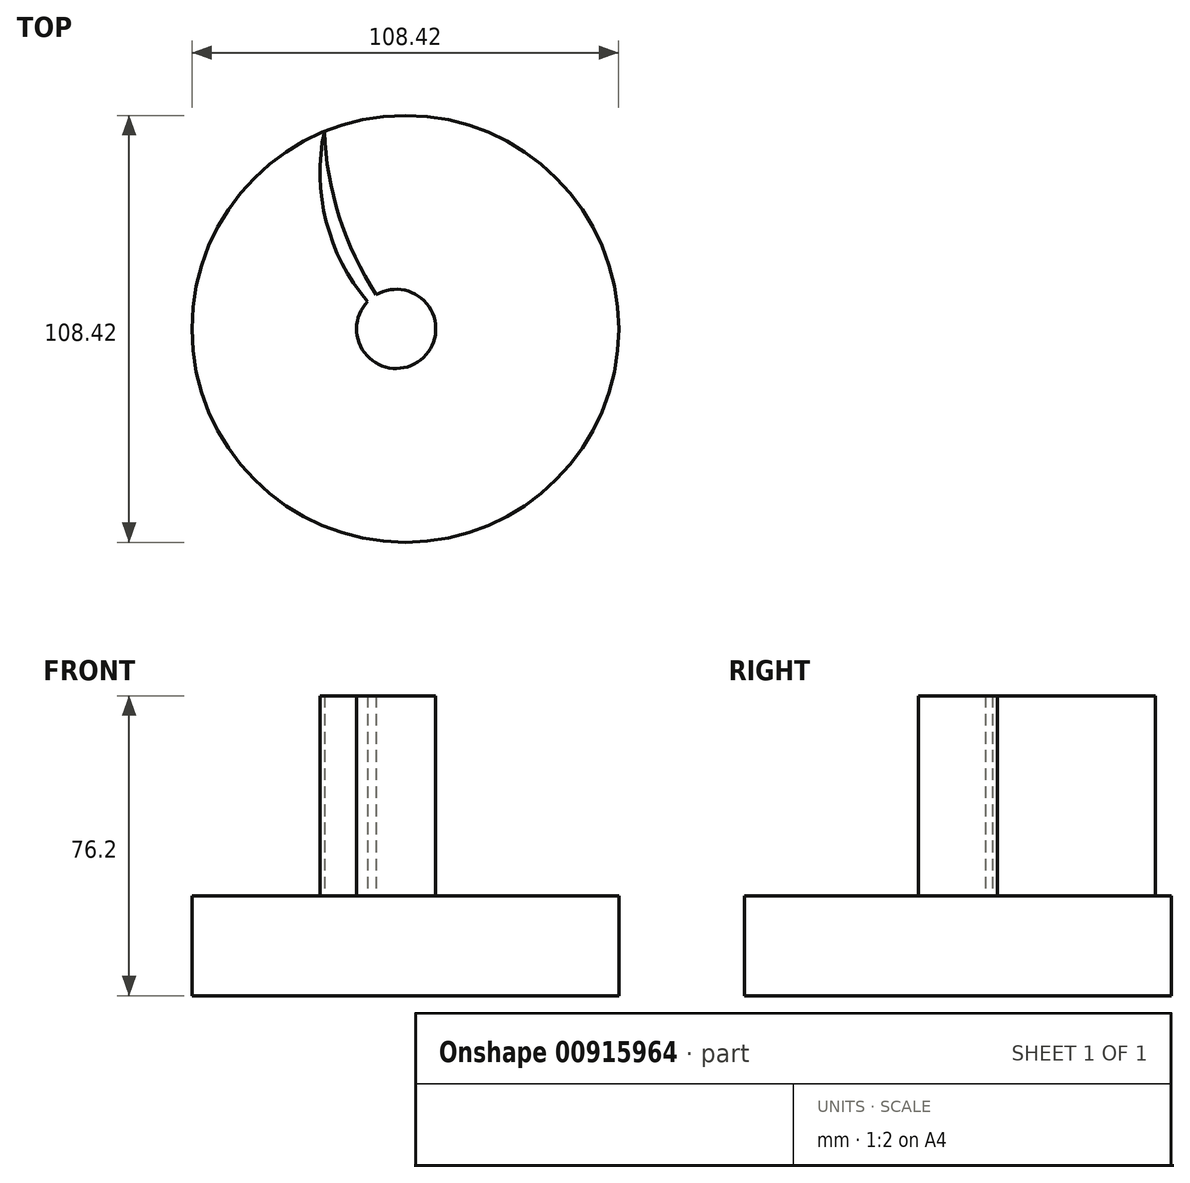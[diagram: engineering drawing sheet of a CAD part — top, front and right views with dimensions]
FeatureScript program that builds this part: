
annotation { "Feature Type Name" : "Feature", "Feature Type Description" : "" }
export const myFeature = defineFeature(function(context is Context, id is Id, definition is map)
    precondition{}
    {
        {
            var Q0;
            Q0=qCreatedBy(makeId("Top.planeOp"),FACE);
            var sketch = newSketch(context, id + "F0", { "sketchPlane" : qUnion([Q0])});
            skCircle(sketch, "E0", {"center": v(0, 0) * mm, "radius": 54.21 * mm});
            skSolve(sketch);
        }
        {
            var Q0;
            Q0=makeQuery(id+"F0.imprint","IMPRINT",FACE,{"disambiguationData":[TD([[makeQuery(id+"F0.imprint","IMPRINT",EDGE,{"derivedFrom":sQuery(id+"F0.wireOp",EDGE,"E0")}),1.0]])]});
            extrude(context, id + "F1", {"entities" : qUnion([Q0]), "depth" : 25.4 * mm, "offsetDistance" : 25.4 * mm});
        }
        {
            var Q0;
            Q0=makeQuery(id+"F1.opExtrude","CAP_FACE",FACE,{"disambiguationData":[OSD([sQuery(id+"F0.wireOp",EDGE,"E0")])],"isStart":false});
            var sketch = newSketch(context, id + "F2", { "sketchPlane" : qUnion([Q0])});
            skArc(sketch, "E1", {"start": v(-20.6, 50.15) * mm, "mid": v(-20.1, 27.28) * mm, "end": v(-9.6, 6.97) * mm});
            skArc(sketch, "E2", {"start": v(-20.6, 50.15) * mm, "mid": v(-16.79, 28.53) * mm, "end": v(-7.42, 8.68) * mm});
            skArc(sketch, "E3", {"start": v(-9.6, 6.97) * mm, "mid": v(3.9, -7.9) * mm, "end": v(-7.42, 8.68) * mm});
            skPoint(sketch, "E4.orphan", {"position": v(0, -1.1) * mm});
            skSolve(sketch);
        }
        {
            var Q0;
            Q0 = qSketchRegion(id + "F2", true);
            extrude(context, id + "F3", {"entities" : qUnion([Q0]), "operationType" : NewBodyOperationType.ADD, "depth" : 50.8 * mm, "offsetDistance" : 25.4 * mm});
        }
    });
